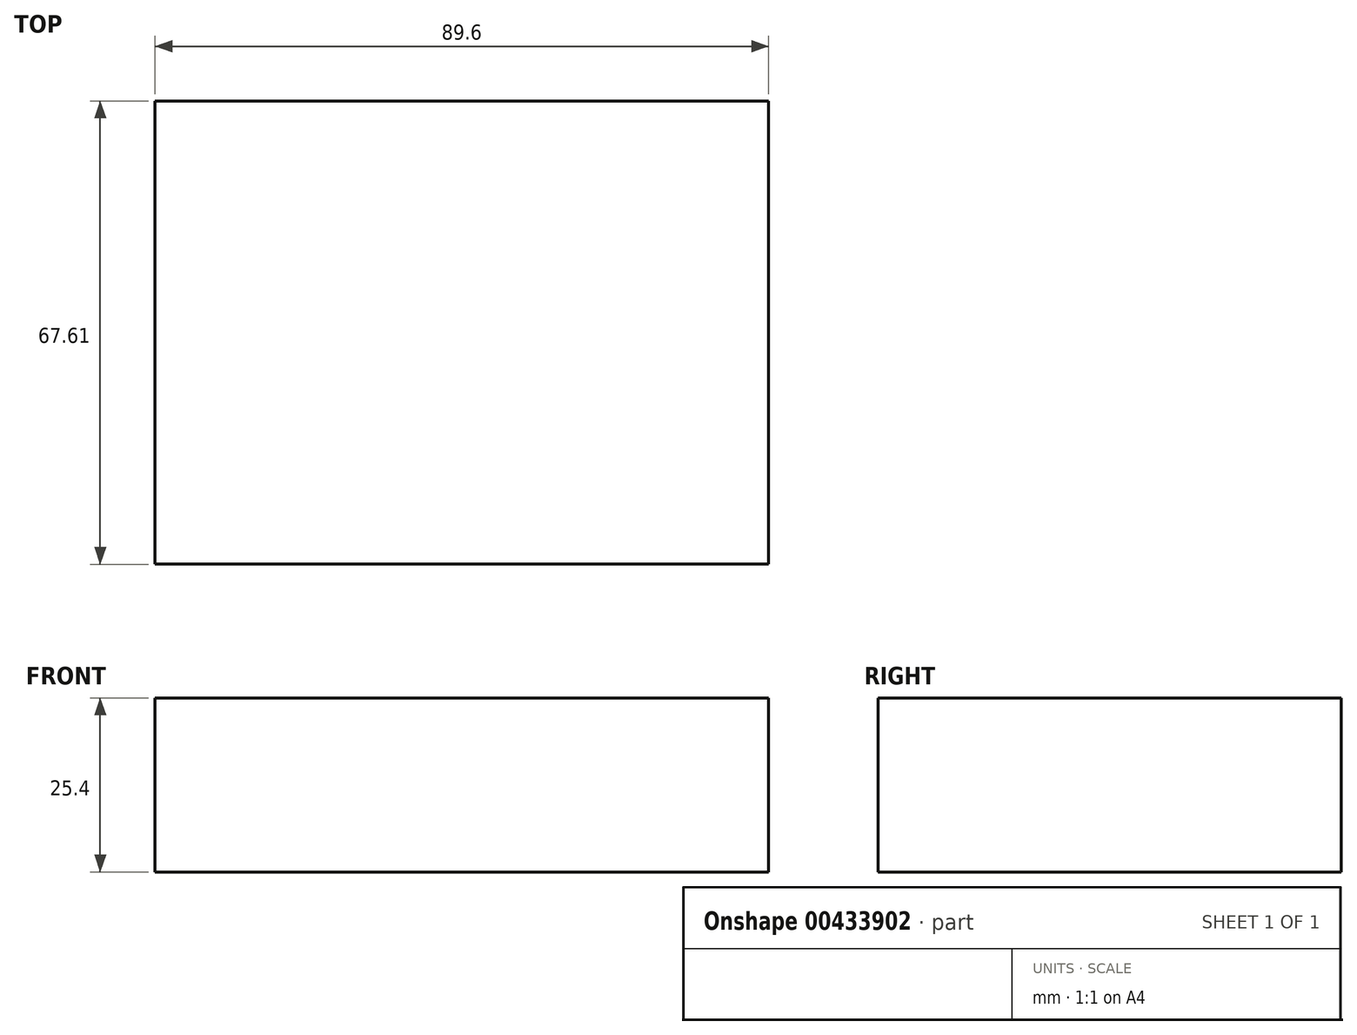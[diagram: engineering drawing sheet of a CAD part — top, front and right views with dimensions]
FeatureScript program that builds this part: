
annotation { "Feature Type Name" : "Feature", "Feature Type Description" : "" }
export const myFeature = defineFeature(function(context is Context, id is Id, definition is map)
    precondition{}
    {
        {
            var Q0;
            Q0=qCreatedBy(makeId("Top.planeOp"),FACE);
            var sketch = newSketch(context, id + "F0", { "sketchPlane" : qUnion([Q0])});
            skLineSegment(sketch, "E0.bottom", {"start": v(-40.28, 43.5) * mm, "end": v(49.32, 43.5) * mm});
            skLineSegment(sketch, "E0.top", {"start": v(-40.28, -24.12) * mm, "end": v(49.32, -24.12) * mm});
            skLineSegment(sketch, "E0.left", {"start": v(-40.28, 43.5) * mm, "end": v(-40.28, -24.12) * mm});
            skLineSegment(sketch, "E0.right", {"start": v(49.32, 43.5) * mm, "end": v(49.32, -24.12) * mm});
            skSolve(sketch);
        }
        {
            var Q0;
            Q0=makeQuery(id+"F0.imprint","IMPRINT",FACE,{"disambiguationData":[TD([[makeQuery(id+"F0.imprint","IMPRINT",EDGE,{"derivedFrom":sQuery(id+"F0.wireOp",EDGE,"E0.bottom")}),-1.0]])]});
            extrude(context, id + "F1", {"entities" : qUnion([Q0]), "depth" : 25.4 * mm});
        }
    });
